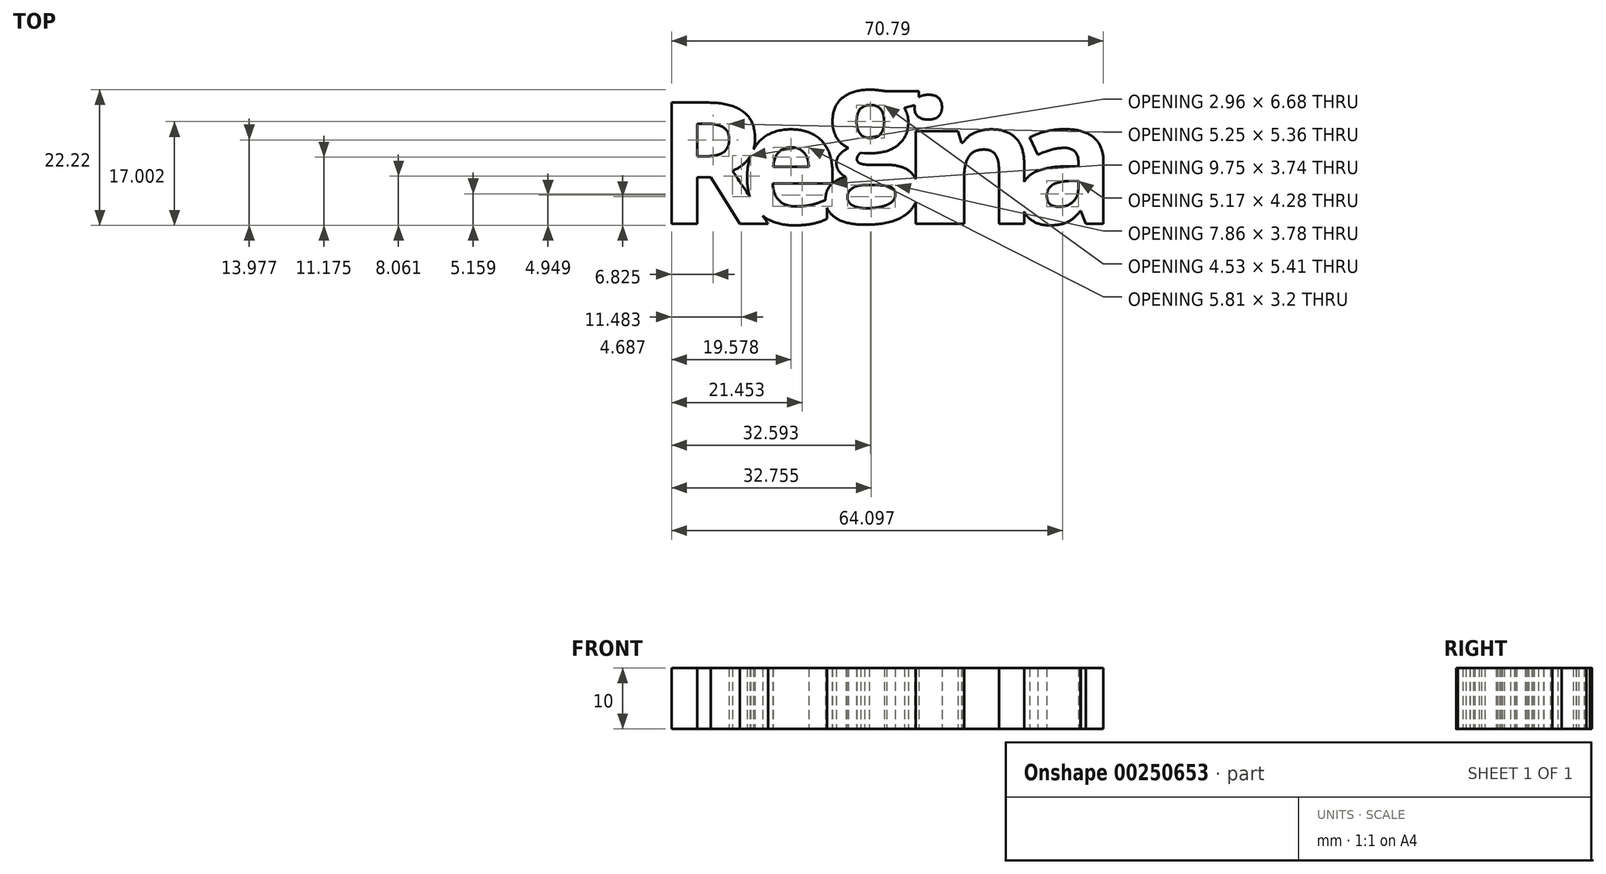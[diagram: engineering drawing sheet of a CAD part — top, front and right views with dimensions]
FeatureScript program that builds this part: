
annotation { "Feature Type Name" : "Feature", "Feature Type Description" : "" }
export const myFeature = defineFeature(function(context is Context, id is Id, definition is map)
    precondition{}
    {
        {
            var Q0;
            Q0=qCreatedBy(makeId("Top.planeOp"),FACE);
            var sketch = newSketch(context, id + "F0", { "sketchPlane" : qUnion([Q0])});
            skText(sketch, "E0", { "text": "R", "fontName": "OpenSans-Bold.ttf"});
            skText(sketch, "E1", { "text": "e", "fontName": "OpenSans-Bold.ttf"});
            skText(sketch, "E2", { "text": "g", "fontName": "OpenSans-Bold.ttf"});
            skText(sketch, "E3", { "text": "i", "fontName": "OpenSans-Bold.ttf"});
            skText(sketch, "E4", { "text": "n", "fontName": "OpenSans-Bold.ttf"});
            skText(sketch, "E5", { "text": "a", "fontName": "OpenSans-Bold.ttf"});
            const initialGuessF0  = {"E0": [-0.09878, 0.04851, 1, 0, 0.02], "E1": [-0.08514, 0.04851, 1, 0, 0.02], "E2": [-0.07112, 0.05501, 1, 0, 0.02], "E3": [-0.05845, 0.04851, 1, 0, 0.02], "E4": [-0.05465, 0.04851, 1, 0, 0.02], "E5": [-0.04018, 0.04851, 1, 0, 0.02]};
            skSetInitialGuess(sketch, initialGuessF0);
            skSolve(sketch);
        }
        {
            var Q0;
            Q0 = qSketchRegion(id + "F0", true);
            extrude(context, id + "F1", {"entities" : qUnion([Q0]), "depth" : 10 * mm});
        }
    });
